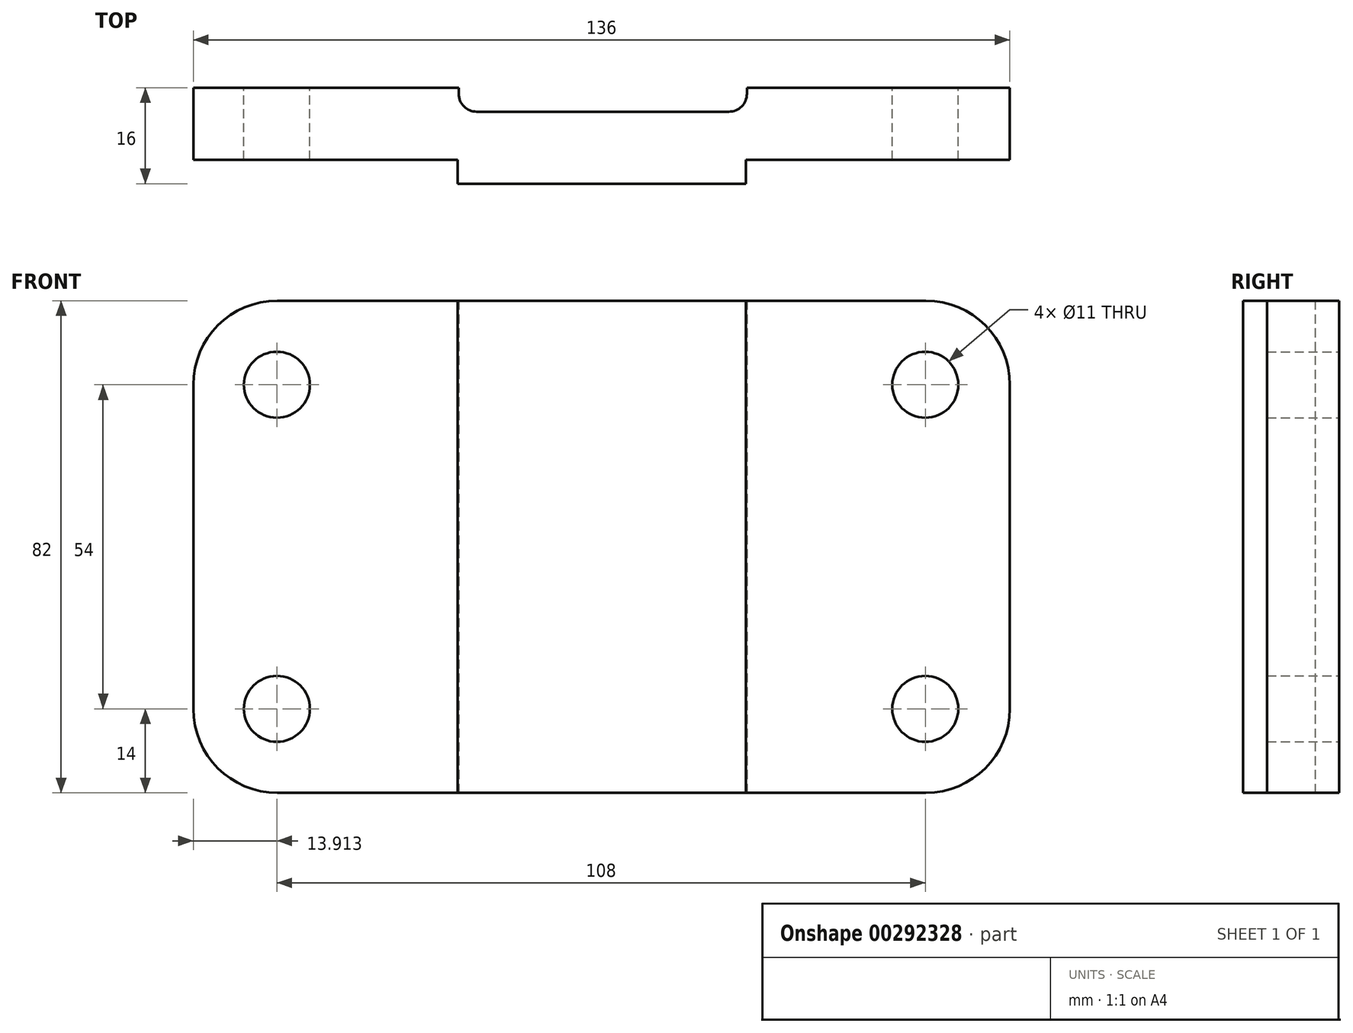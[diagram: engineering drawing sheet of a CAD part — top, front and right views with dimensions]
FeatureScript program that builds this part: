
annotation { "Feature Type Name" : "Feature", "Feature Type Description" : "" }
export const myFeature = defineFeature(function(context is Context, id is Id, definition is map)
    precondition{}
    {
        {
            var Q0;
            Q0=qCreatedBy(makeId("Front.planeOp"),FACE);
            var sketch = newSketch(context, id + "F0", { "sketchPlane" : qUnion([Q0])});
            skLineSegment(sketch, "E0.bottom", {"start": v(0, 0) * mm, "end": v(136, 0) * mm});
            skLineSegment(sketch, "E0.top", {"start": v(0, 82) * mm, "end": v(136, 82) * mm});
            skLineSegment(sketch, "E0.left", {"start": v(0, 0) * mm, "end": v(0, 82) * mm});
            skLineSegment(sketch, "E0.right", {"start": v(136, 0) * mm, "end": v(136, 82) * mm});
            skSolve(sketch);
        }
        {
            var Q0;
            Q0 = qSketchRegion(id + "F0", true);
            extrude(context, id + "F1", {"entities" : qUnion([Q0]), "depth" : 12 * mm});
        }
        {
            var Q0;
            Q0=makeQuery(id+"F1.opExtrude","CAP_FACE",FACE,{"disambiguationData":[OSD([sQuery(id+"F0.wireOp",EDGE,"E0.bottom"),sQuery(id+"F0.wireOp",EDGE,"E0.top"),sQuery(id+"F0.wireOp",EDGE,"E0.left"),sQuery(id+"F0.wireOp",EDGE,"E0.right")])],"isStart":false});
            var sketch = newSketch(context, id + "F2", { "sketchPlane" : qUnion([Q0])});
            skLineSegment(sketch, "E1.bottom", {"start": v(0, 0) * mm, "end": v(44, 0) * mm});
            skLineSegment(sketch, "E1.top", {"start": v(0, 82) * mm, "end": v(44, 82) * mm});
            skLineSegment(sketch, "E1.left", {"start": v(0, 0) * mm, "end": v(0, 82) * mm});
            skLineSegment(sketch, "E1.right", {"start": v(44, 0) * mm, "end": v(44, 82) * mm});
            skLineSegment(sketch, "E2.bottom", {"start": v(136, 0) * mm, "end": v(92, 0) * mm});
            skLineSegment(sketch, "E2.top", {"start": v(136, 82) * mm, "end": v(92, 82) * mm});
            skLineSegment(sketch, "E2.left", {"start": v(136, 0) * mm, "end": v(136, 82) * mm});
            skLineSegment(sketch, "E2.right", {"start": v(92, 0) * mm, "end": v(92, 82) * mm});
            skLineSegment(sketch, "E3.bottom", {"start": v(44, 82) * mm, "end": v(92, 82) * mm});
            skLineSegment(sketch, "E3.top", {"start": v(44, 0) * mm, "end": v(92, 0) * mm});
            skLineSegment(sketch, "E3.left", {"start": v(44, 82) * mm, "end": v(44, 0) * mm});
            skLineSegment(sketch, "E3.right", {"start": v(92, 82) * mm, "end": v(92, 0) * mm});
            skSolve(sketch);
        }
        {
            var Q0;
            Q0=makeQuery(id+"F2.imprint","IMPRINT",FACE,{"disambiguationData":[TD([[makeQuery(id+"F2.imprint","IMPRINT",EDGE,{"derivedFrom":sQuery(id+"F2.wireOp",EDGE,"E3.bottom")}),-1.0]])]});
            extrude(context, id + "F3", {"entities" : qUnion([Q0]), "operationType" : NewBodyOperationType.ADD, "depth" : 4 * mm});
        }
        {
            var Q0;
            Q0=makeQuery(id+"F1.opExtrude","CAP_FACE",FACE,{"disambiguationData":[OSD([sQuery(id+"F0.wireOp",EDGE,"E0.bottom"),sQuery(id+"F0.wireOp",EDGE,"E0.top"),sQuery(id+"F0.wireOp",EDGE,"E0.left"),sQuery(id+"F0.wireOp",EDGE,"E0.right")])],"isStart":true});
            var sketch = newSketch(context, id + "F4", { "sketchPlane" : qUnion([Q0])});
            skLineSegment(sketch, "E4.bottom", {"start": v(-92.2, 82) * mm, "end": v(-44.2, 82) * mm});
            skLineSegment(sketch, "E4.top", {"start": v(-92.2, 0) * mm, "end": v(-44.2, 0) * mm});
            skLineSegment(sketch, "E4.left", {"start": v(-92.2, 82) * mm, "end": v(-92.2, 0) * mm});
            skLineSegment(sketch, "E4.right", {"start": v(-44.2, 82) * mm, "end": v(-44.2, 0) * mm});
            skSolve(sketch);
        }
        {
            var Q0;
            Q0=makeQuery(id+"F4.imprint","IMPRINT",FACE,{"disambiguationData":[TD([[makeQuery(id+"F4.imprint","IMPRINT",EDGE,{"derivedFrom":sQuery(id+"F4.wireOp",EDGE,"E4.bottom")}),1.0]])]});
            extrude(context, id + "F5", {"entities" : qUnion([Q0]), "operationType" : NewBodyOperationType.REMOVE, "oppositeDirection" : true, "depth" : 4 * mm});
        }
        {
            var Q0;
            Q0=makeQuery(id+"F1.opExtrude","SWEPT_EDGE",EDGE,{"disambiguationData":[OSD([sQuery(id+"F0.wireOp",EDGE,"E0.top"),sQuery(id+"F0.wireOp",EDGE,"E0.right")])]});
            var Q1;
            Q1=makeQuery(id+"F1.opExtrude","SWEPT_EDGE",EDGE,{"disambiguationData":[OSD([sQuery(id+"F0.wireOp",EDGE,"E0.top"),sQuery(id+"F0.wireOp",EDGE,"E0.left")])]});
            var Q2;
            Q2=makeQuery(id+"F1.opExtrude","SWEPT_EDGE",EDGE,{"disambiguationData":[OSD([sQuery(id+"F0.wireOp",EDGE,"E0.bottom"),sQuery(id+"F0.wireOp",EDGE,"E0.right")])]});
            var Q3;
            Q3=makeQuery(id+"F1.opExtrude","SWEPT_EDGE",EDGE,{"disambiguationData":[OSD([sQuery(id+"F0.wireOp",EDGE,"E0.bottom"),sQuery(id+"F0.wireOp",EDGE,"E0.left")])]});
            fillet(context, id + "F6", {"entities" : qUnion([Q0, Q1, Q2, Q3]), "radius" : 14 * mm, "tangentPropagation" : true, "allowEdgeOverflow" : false});
        }
        {
            var Q0;
            Q0=qCreatedBy(makeId("Front.planeOp"),FACE);
            var sketch = newSketch(context, id + "F7", { "sketchPlane" : qUnion([Q0])});
            skLineSegment(sketch, "E5", {"start": v(0, 14) * mm, "end": v(148.92, 14) * mm, "construction": true});
            skLineSegment(sketch, "E6", {"start": v(0, 68) * mm, "end": v(146.13, 68) * mm, "construction": true});
            skLineSegment(sketch, "E7", {"start": v(13.91, 85.39) * mm, "end": v(13.91, 0) * mm, "construction": true});
            skLineSegment(sketch, "E8", {"start": v(121.91, 85.06) * mm, "end": v(121.91, 0) * mm});
            skCircle(sketch, "E9", {"center": v(13.91, 68) * mm, "radius": 5.5 * mm});
            skCircle(sketch, "E10", {"center": v(13.91, 14) * mm, "radius": 5.5 * mm});
            skCircle(sketch, "E11", {"center": v(121.91, 68) * mm, "radius": 5.5 * mm});
            skCircle(sketch, "E12", {"center": v(121.91, 14) * mm, "radius": 5.5 * mm});
            skSolve(sketch);
        }
        {
            var Q0;
            {var subQ0=sQuery(id+"F7.wireOp",EDGE,"E11");var subQ1=sQuery(id+"F7.wireOp",EDGE,"E8");var subQ2=makeQuery(id+"F7.imprint","INTERSECT",VERTEX,{"disambiguationData":[OD(0.0)],"derivedFrom":[subQ1,subQ0]});Q0=makeQuery(id+"F7.imprint","IMPRINT",FACE,{"disambiguationData":[TD([[makeQuery(id+"F7.imprint","IMPRINT",EDGE,{"disambiguationData":[TD([[subQ2,1.0]])],"derivedFrom":subQ1}),-1.0]])]});}
            var Q1;
            {var subQ0=sQuery(id+"F7.wireOp",EDGE,"E11");var subQ1=sQuery(id+"F7.wireOp",EDGE,"E8");var subQ2=makeQuery(id+"F7.imprint","INTERSECT",VERTEX,{"disambiguationData":[OD(0.0)],"derivedFrom":[subQ1,subQ0]});Q1=makeQuery(id+"F7.imprint","IMPRINT",FACE,{"disambiguationData":[TD([[makeQuery(id+"F7.imprint","IMPRINT",EDGE,{"disambiguationData":[TD([[subQ2,1.0]])],"derivedFrom":subQ1}),1.0]])]});}
            var Q2;
            {var subQ0=sQuery(id+"F7.wireOp",EDGE,"E12");var subQ1=sQuery(id+"F7.wireOp",EDGE,"E8");var subQ2=makeQuery(id+"F7.imprint","INTERSECT",VERTEX,{"disambiguationData":[OD(0.0)],"derivedFrom":[subQ1,subQ0]});Q2=makeQuery(id+"F7.imprint","IMPRINT",FACE,{"disambiguationData":[TD([[makeQuery(id+"F7.imprint","IMPRINT",EDGE,{"disambiguationData":[TD([[subQ2,1.0]])],"derivedFrom":subQ1}),1.0]])]});}
            var Q3;
            {var subQ0=sQuery(id+"F7.wireOp",EDGE,"E12");var subQ1=sQuery(id+"F7.wireOp",EDGE,"E8");var subQ2=makeQuery(id+"F7.imprint","INTERSECT",VERTEX,{"disambiguationData":[OD(0.0)],"derivedFrom":[subQ1,subQ0]});Q3=makeQuery(id+"F7.imprint","IMPRINT",FACE,{"disambiguationData":[TD([[makeQuery(id+"F7.imprint","IMPRINT",EDGE,{"disambiguationData":[TD([[subQ2,1.0]])],"derivedFrom":subQ1}),-1.0]])]});}
            var Q4;
            Q4=makeQuery(id+"F7.imprint","IMPRINT",FACE,{"disambiguationData":[TD([[makeQuery(id+"F7.imprint","IMPRINT",EDGE,{"derivedFrom":sQuery(id+"F7.wireOp",EDGE,"E10")}),1.0]])]});
            var Q5;
            Q5=makeQuery(id+"F7.imprint","IMPRINT",FACE,{"disambiguationData":[TD([[makeQuery(id+"F7.imprint","IMPRINT",EDGE,{"derivedFrom":sQuery(id+"F7.wireOp",EDGE,"E9")}),1.0]])]});
            extrude(context, id + "F8", {"entities" : qUnion([Q0, Q1, Q2, Q3, Q4, Q5]), "operationType" : NewBodyOperationType.REMOVE, "endBound" : BoundingType.THROUGH_ALL, "depth" : 25 * mm});
        }
        {
            var Q0;
            Q0=makeQuery(id+"F5.boolean.opBoolean","COPY",EDGE,{"derivedFrom":makeQuery(id+"F5.opExtrude","CAP_EDGE",EDGE,{"disambiguationData":[OSD([sQuery(id+"F4.wireOp",EDGE,"E4.left")])],"isStart":false})});
            var Q1;
            Q1=makeQuery(id+"F5.boolean.opBoolean","COPY",EDGE,{"derivedFrom":makeQuery(id+"F5.opExtrude","CAP_EDGE",EDGE,{"disambiguationData":[OSD([sQuery(id+"F4.wireOp",EDGE,"E4.right")])],"isStart":false})});
            fillet(context, id + "F9", {"entities" : qUnion([Q0, Q1]), "radius" : 3 * mm, "tangentPropagation" : true, "allowEdgeOverflow" : false});
        }
    });
